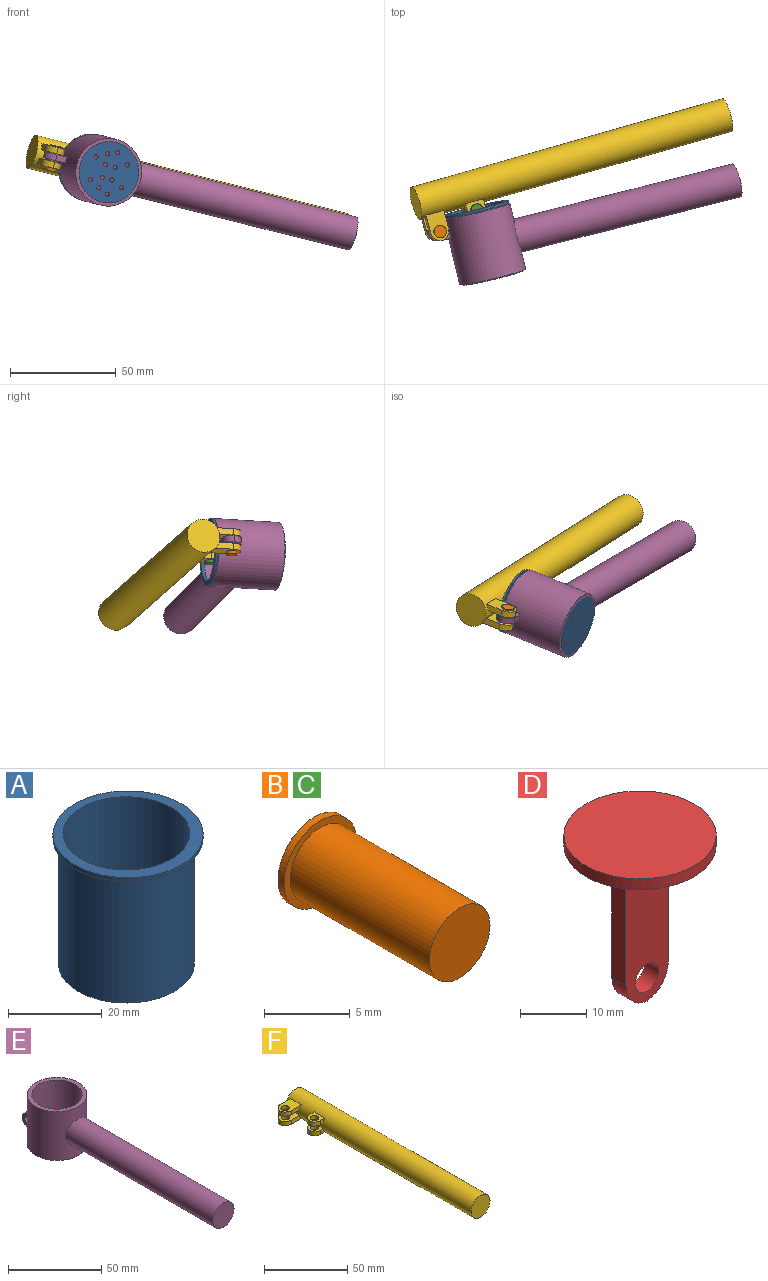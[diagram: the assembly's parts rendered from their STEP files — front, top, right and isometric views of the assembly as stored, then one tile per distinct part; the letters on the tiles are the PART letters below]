
ASSEMBLY  parts=6 mates=5
PART A: 19 faces, bbox 32x32x34 mm
  f0: cylinder r=14.5mm len=33mm, axis (0,0,-1), area 3006.5mm2, adj f1,f18
  f1: plane 29x29mm, normal (0,0,-1), area 622.8mm2, adj f0,f5,f6,f7,f8,f9,f10,f11
  f2: plane 27x27mm, normal (0,0,1), area 534.9mm2, adj f3,f5,f6,f7,f8,f9,f10,f11
  f3: cylinder r=13.5mm len=33mm, axis (0,0,-1), area 2799.2mm2, adj f2,f4
  f4: plane 32x32mm, normal (0,0,1), area 231.7mm2, adj f3,f17
  f5: cylinder r=1mm len=2mm, axis (0,0,-1), area 6.3mm2, adj f1,f2
  f6: cylinder r=1mm len=2mm, axis (0,0,-1), area 6.3mm2, adj f1,f2
  f7: cylinder r=1mm len=2mm, axis (0,0,-1), area 6.3mm2, adj f1,f2
  f8: cylinder r=1mm len=2mm, axis (0,0,-1), area 6.3mm2, adj f1,f2
  f9: cylinder r=1mm len=2mm, axis (0,0,-1), area 6.3mm2, adj f1,f2
  f10: cylinder r=1mm len=2mm, axis (0,0,-1), area 6.3mm2, adj f1,f2
  f11: cylinder r=1mm len=2mm, axis (0,0,-1), area 6.3mm2, adj f1,f2
  f12: cylinder r=1mm len=2mm, axis (0,0,-1), area 6.3mm2, adj f1,f2
  f13: cylinder r=1mm len=2mm, axis (0,0,-1), area 6.3mm2, adj f1,f2
  f14: cylinder r=1mm len=2mm, axis (0,0,-1), area 6.3mm2, adj f1,f2
  f15: cylinder r=1mm len=2mm, axis (0,0,-1), area 6.3mm2, adj f1,f2
  f16: cylinder r=1mm len=2mm, axis (0,0,-1), area 6.3mm2, adj f1,f2
  f17: cylinder r=16mm len=32mm, axis (0,0,1), area 100.5mm2, adj f4,f18
  f18: plane 32x32mm, normal (0,0,-1), area 143.7mm2, adj f0,f17
PART B: 5 faces, bbox 6x12x6 mm
  f0: cylinder r=2.5mm len=11.5mm, axis (0,1,0), area 180.6mm2, adj f1,f3
  f1: plane 5x5mm, normal (0,-1,0), area 19.6mm2, adj f0
  f2: cylinder r=3mm len=6mm, axis (0,1,0), area 9.4mm2, adj f3,f4
  f3: plane 6x6mm, normal (0,-1,0), area 8.6mm2, adj f0,f2
  f4: plane 6x6mm, normal (0,1,0), area 28.3mm2, adj f2
PART C: same geometry as B
PART D: 10 faces, bbox 23x23x30 mm
  f0: cylinder r=11.5mm len=23mm, axis (0,0,-1), area 144.5mm2, adj f1,f2
  f1: plane 23x23mm, normal (0,0,1), area 415.5mm2, adj f0
  f2: plane 23x23mm, normal (0,0,-1), area 388.5mm2, adj f0,f3,f4,f5,f6
  f3: plane 27.98x9mm, normal (0,-1,0), area 221.6mm2, adj f2,f4,f6,f7,f8,f9
  f4: plane 23x3mm, normal (-1,0,0), area 69mm2, adj f2,f3,f5,f9
  f5: plane 27.98x9mm, normal (0,1,0), area 221.6mm2, adj f2,f4,f6,f7,f8,f9
  f6: plane 23x3mm, normal (1,0,0), area 69mm2, adj f2,f3,f5,f8
  f7: cylinder r=2.5mm len=5mm, axis (0,-1,0), area 47.1mm2, adj f3,f5
  f8: cylinder r=5mm len=4.98mm, axis (0,1,0), area 22.1mm2, adj f3,f5,f6,f9
  f9: cylinder r=5mm len=4.98mm, axis (0,-1,0), area 22.1mm2, adj f3,f4,f5,f8
PART E: 15 faces, bbox 32x151.9x32 mm
  f0: cylinder r=16mm len=32mm, axis (0,0,-1), area 2985.6mm2, adj f1,f2,f3,f6,f7,f8,f9,f10
  f1: cylinder r=8mm len=112mm, axis (0,1,0), area 5585.8mm2, adj f0,f2,f3,f4
  f2: plane 5.31x0.45mm, normal (0,1,0), area 1.6mm2, adj f0,f1
  f3: plane 5.31x0.45mm, normal (0,1,0), area 1.6mm2, adj f0,f1
  f4: plane 16x16mm, normal (0,-1,0), area 201.1mm2, adj f1
  f5: cylinder r=13.5mm len=32mm, axis (0,0,-1), area 2714.3mm2, adj f6,f7
  f6: plane 32x32mm, normal (0,0,1), area 231.7mm2, adj f0,f5
  f7: plane 32x32mm, normal (0,0,-1), area 231.7mm2, adj f0,f5
  f8: plane 9.92x9mm, normal (1,0,0), area 59.2mm2, adj f0,f10,f11,f12,f13,f14
  f9: plane 9.79x9mm, normal (-1,0,0), area 57.9mm2, adj f0,f10,f11,f12,f13,f14
  f10: plane 4.95x3mm, normal (0,0,1), area 14.5mm2, adj f0,f8,f9,f14
  f11: plane 4.95x3mm, normal (0,0,-1), area 14.5mm2, adj f0,f8,f9,f13
  f12: cylinder r=2.5mm len=5mm, axis (-1,0,0), area 47.1mm2, adj f8,f9
  f13: cylinder r=5mm len=4.98mm, axis (-1,0,0), area 22.1mm2, adj f8,f9,f11,f14
  f14: cylinder r=5mm len=4.98mm, axis (1,0,0), area 22.1mm2, adj f8,f9,f10,f13
PART F: 31 faces, bbox 28x157x16 mm
  f0: cylinder r=8mm len=157mm, axis (0,1,0), area 7769.7mm2, adj f1,f2,f3,f4,f5,f6,f7,f8
  f1: plane 16x16mm, normal (0,-1,0), area 201.1mm2, adj f0
  f2: plane 16x16mm, normal (0,1,0), area 201.1mm2, adj f0
  f3: plane 9x7.25mm, normal (0,0,-1), area 35.1mm2, adj f0,f5,f6,f12,f15,f16
  f4: plane 9x8.78mm, normal (0,0,1), area 48.9mm2, adj f0,f5,f6,f12,f15,f16
  f5: plane 3.8x3mm, normal (0,1,0), area 8.7mm2, adj f0,f3,f4,f16
  f6: plane 3.8x3mm, normal (0,-1,0), area 8.7mm2, adj f0,f3,f4,f15
  f7: plane 9x7.25mm, normal (0,0,1), area 35.1mm2, adj f0,f9,f10,f11,f13,f14
  f8: plane 9x8.78mm, normal (0,0,-1), area 48.9mm2, adj f0,f9,f10,f11,f13,f14
  f9: plane 3.8x3mm, normal (0,1,0), area 8.7mm2, adj f0,f7,f8,f13
  f10: plane 3.8x3mm, normal (0,-1,0), area 8.7mm2, adj f0,f7,f8,f14
  f11: cylinder r=2.5mm len=5mm, axis (0,0,1), area 47.1mm2, adj f7,f8
  f12: cylinder r=2.5mm len=5mm, axis (0,0,1), area 47.1mm2, adj f3,f4
  f13: cylinder r=5mm len=4.98mm, axis (0,0,-1), area 22.1mm2, adj f7,f8,f9,f14
  f14: cylinder r=5mm len=4.98mm, axis (0,0,1), area 22.1mm2, adj f7,f8,f10,f13
  f15: cylinder r=5mm len=4.98mm, axis (0,0,1), area 22.1mm2, adj f3,f4,f6,f16
  f16: cylinder r=5mm len=4.98mm, axis (0,0,-1), area 22.1mm2, adj f3,f4,f5,f15
  f17: plane 13.66x9mm, normal (0,0,1), area 92.8mm2, adj f0,f19,f20,f27,f28,f30
  f18: plane 12.21x9mm, normal (0,0,-1), area 79.7mm2, adj f0,f19,f20,f27,f28,f30
  f19: plane 8.69x3mm, normal (0,1,0), area 23.5mm2, adj f0,f17,f18,f27
  f20: plane 8.69x3mm, normal (0,-1,0), area 23.5mm2, adj f0,f17,f18,f28
  f21: plane 12.25x9mm, normal (0,0,1), area 80.1mm2, adj f0,f23,f24,f25,f26,f29
  f22: plane 13.8x9mm, normal (0,0,-1), area 94.1mm2, adj f0,f23,f24,f25,f26,f29
  f23: plane 8.83x3mm, normal (0,1,0), area 23.7mm2, adj f0,f21,f22,f25
  f24: plane 8.83x3mm, normal (0,-1,0), area 23.7mm2, adj f0,f21,f22,f26
  f25: cylinder r=5mm len=4.98mm, axis (0,0,-1), area 22.1mm2, adj f21,f22,f23,f26
  f26: cylinder r=5mm len=4.98mm, axis (0,0,1), area 22.1mm2, adj f21,f22,f24,f25
  f27: cylinder r=5mm len=4.98mm, axis (0,0,-1), area 22.1mm2, adj f17,f18,f19,f28
  f28: cylinder r=5mm len=4.98mm, axis (0,0,1), area 22.1mm2, adj f17,f18,f20,f27
  f29: cylinder r=2.5mm len=5mm, axis (0,0,-1), area 47.1mm2, adj f21,f22
  f30: cylinder r=2.5mm len=5mm, axis (0,0,-1), area 47.1mm2, adj f17,f18
PLACE A rot(axis=(-0.62,-0.62,-0.48),103.3deg) t=(45.35,8.97,22.17)mm
PLACE B rot(axis=(0.97,0.25,0.01),93.8deg) t=(36.34,-28.19,30.57)mm
PLACE C rot(axis=(0.97,0.25,0.01),93.8deg) t=(53.73,-18.1,26.36)mm
PLACE D rot(axis=(-0.19,0.71,-0.68),177.7deg) t=(43.25,18.37,22.58)mm
PLACE E rot(axis=(0.71,-0.43,0.55),121.8deg) t=(54.82,28.36,19.8)mm
PLACE F rot(axis=(0.12,0.09,0.99),106.1deg) t=(9.04,44.09,31.91)mm fixed
MATE revolute E.f12 <-> B.f0  axis (-0.24,0,-0.97) through (19.24,30.84,29.5)mm
MATE revolute D.f7 <-> C.f0  axis (0.24,0,0.97) through (36.38,40.93,24.32)mm
MATE fastened B.f0 <-> F.f29  axis (0.24,0,0.97) through (20.4,30.84,34.11)mm
MATE fastened C.f0 <-> F.f11  axis (0.24,0,0.97) through (37.79,40.93,29.9)mm
MATE fastened A.f0 <-> E.f0  axis (0.23,-0.97,-0.06) through (41.54,24.99,23.14)mm
